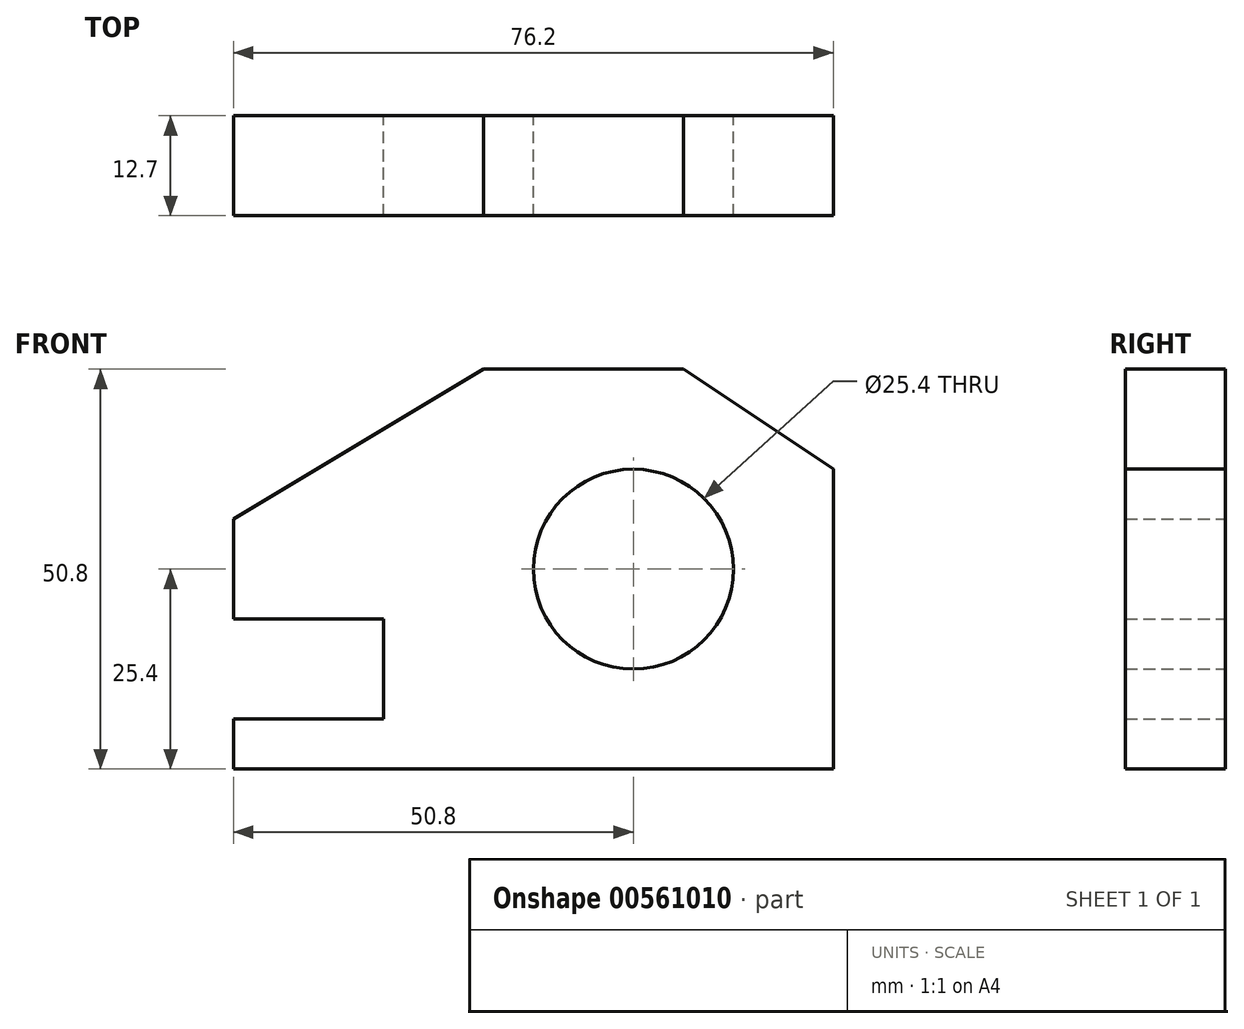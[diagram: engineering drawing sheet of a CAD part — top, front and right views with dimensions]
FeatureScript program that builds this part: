
annotation { "Feature Type Name" : "Feature", "Feature Type Description" : "" }
export const myFeature = defineFeature(function(context is Context, id is Id, definition is map)
    precondition{}
    {
        {
            var Q0;
            Q0=qCreatedBy(makeId("Front.planeOp"),FACE);
            var sketch = newSketch(context, id + "F0", { "sketchPlane" : qUnion([Q0])});
            skLineSegment(sketch, "E0.bottom", {"start": v(0, 0) * mm, "end": v(76.2, 0) * mm});
            skLineSegment(sketch, "E0.top", {"start": v(31.75, 50.8) * mm, "end": v(57.15, 50.8) * mm});
            skLineSegment(sketch, "E0.left", {"start": v(0, 0) * mm, "end": v(0, 6.35) * mm});
            skLineSegment(sketch, "E0.right", {"start": v(76.2, 0) * mm, "end": v(76.2, 38.1) * mm});
            skLineSegment(sketch, "E1", {"start": v(57.15, 50.8) * mm, "end": v(76.2, 38.1) * mm});
            skLineSegment(sketch, "E2", {"start": v(57.15, 50.8) * mm, "end": v(31.75, 50.8) * mm});
            skLineSegment(sketch, "E3", {"start": v(0, 31.75) * mm, "end": v(31.75, 50.8) * mm});
            skLineSegment(sketch, "E4.bottom", {"start": v(0, 6.35) * mm, "end": v(19.05, 6.35) * mm});
            skLineSegment(sketch, "E4.top", {"start": v(0, 19.05) * mm, "end": v(19.05, 19.05) * mm});
            skLineSegment(sketch, "E4.right", {"start": v(19.05, 6.35) * mm, "end": v(19.05, 19.05) * mm});
            skLineSegment(sketch, "E5.bottom", {"start": v(76.2, 0) * mm, "end": v(50.8, 0) * mm});
            skLineSegment(sketch, "E5.left", {"start": v(76.2, 0) * mm, "end": v(76.2, 25.4) * mm});
            skCircle(sketch, "E6", {"center": v(50.8, 25.4) * mm, "radius": 12.7 * mm});
            skLineSegment(sketch, "E7.trimOffspring", {"start": v(0, 19.05) * mm, "end": v(0, 31.75) * mm});
            skSolve(sketch);
        }
        {
            var Q0;
            Q0=makeQuery(id+"F0.imprint","IMPRINT",FACE,{"disambiguationData":[TD([[makeQuery(id+"F0.imprint","IMPRINT",EDGE,{"derivedFrom":sQuery(id+"F0.wireOp",EDGE,"E0.bottom")}),1.0]])]});
            extrude(context, id + "F1", {"entities" : qUnion([Q0]), "depth" : 12.7 * mm, "offsetDistance" : 25.4 * mm});
        }
    });
